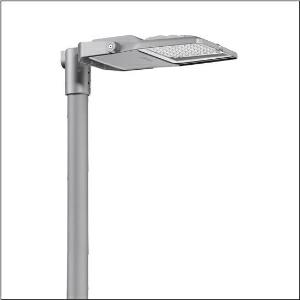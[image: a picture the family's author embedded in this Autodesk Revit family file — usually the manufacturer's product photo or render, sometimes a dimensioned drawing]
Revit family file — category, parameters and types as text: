
# Revit family: floodlight_fl_21_iq_mini___pl61_5xa7772b4c3a_beff
name_source: partatom
category: Lighting Fixtures
units: mm (PartAtom-declared; Revit-internal decimal feet)

## family parameters
Cut with Voids When Loaded = No
Host = Face
Light Source = No
Part Type = Normal
Room Calculation Point = No
Round Connector Dimension = Use Diameter
Shared = No

## types (1)
- --- (1 x LED, 6370 lm, 45.5 W, 4000K)
    Apparent Load = 46 VA
    CIE Flux Codes = 33 65 98 100 100
    Color Rendering = 70
    Color Temperature = 4000K
    Default Elevation = 1800 mm
    Description = Floodlight FL 21 iQ mini, floodlight, primary light control with lens, of PMMA, primary optical cover: protective disc, of toughened safety glass, transparent, light distribution: PL61, light emission: direct distribution, installation type: surface-mounted, lamps: LED, High Power LED, rated values: 6.370lm | 45,5W | 140lm/W (begin service life); end service life: 6.370lm | 48W; at 50% lumin. flux: 3.185lm | 21,5W | 148,1lm/W, colour temperature: 4000K, colour rendering: CRI > 70, light colour: 740, light setting 1 begin service life: 100% | 6.370lm | 45,5W | 140lm/W | 4.000K, light setting 1 end service life: 48W, further light settings possible, control: pre-setting: linear dimming characteristic, Auto-Match, Temp-Guard, Night-Set, Smart-Wire, Desk-Remote (wireless, voltage-free reading and setting of iQ features in the workshop via application-optimized NFC function/RFID function), optimised constant luminous flux control (CLO 2.0), Light-Fading, Lumen-Switch, with terminal, 6-pole, mains connection: 220..240V, AC, 50/60Hz, luminaire housing, of diecast aluminium, powder-coated, SITECO metallic grey (DB 702S), corrosivity category C5 mid according to DIN EN ISO 12944suitable for swimming poolschlorine-resistant, sealing non-destructively replaceable, please order mast flange separately, mast bracket, of steel, galvanised, powder-coated, protection rating (complete): IP66, insulation class (complete): insulation class II (safety insulation), certification: CE, ENEC, VDE, protection symbol: D, impact resistance: IK08, permissible operating ambient temperature: -40..+40°C, permissible operating ambient temperature for outdoor applications: -40..+50°C, standard: DIN EN 12944, LABS conformity tested according to VDMA 24364:2018-05, packaging unit: 1 piece

Light Distribution: PL61
    Height = 70 mm
    Lamp = 1 x LED
    Lamp Light Flux = 6370 lm
    Lamp Power = 45.5 W
    Lamp count = 1
    Length = 485 mm
    Luminous efficacy = 140 lm/W
    Manufacturer = Siteco
    ModVariant = No
    Model = 5XA7772B4C3A
    Mounting Place = Pole
    Mounting Type = Pole annexe
    Number of Poles = 1
    OnlyDefault = Yes
    Power Factor = 1
    Product Name = Floodlight FL 21 iQ mini | PL61
    Product group = floodlight | pylon annexe
    ProductGroupID = 6201
    Protection Class = Protection class II
    Protection Degree = IP 66
    RLX_Detail_Level = 1
    RLX_Emergency_Light_Flux = 0 lm
    RLX_Emergency_Type = 0
    RLX_Emergency_Type_DB = No
    RlxData = <blob elided: 101513 chars, md5=dcb9044e>
    Socket = socket
    Standby Power = 0 W
    System Light Flux = 6370 lm
    System Power = 46 W
    Type Comments = factory setting: luminous flux: 100 % | dim-lin: 254 | 463 mA
    Type Image = l_1007125.jpg
    URL = http://relux.com
    VarID = @adj_174481
    Voltage = 0 V
    Weight = 0.00 kg
    Width = 337 mm

## geometry (parser evidence)
native form markers: Blend x4, Sweep x12
no freeform markers — native parametric forms only
